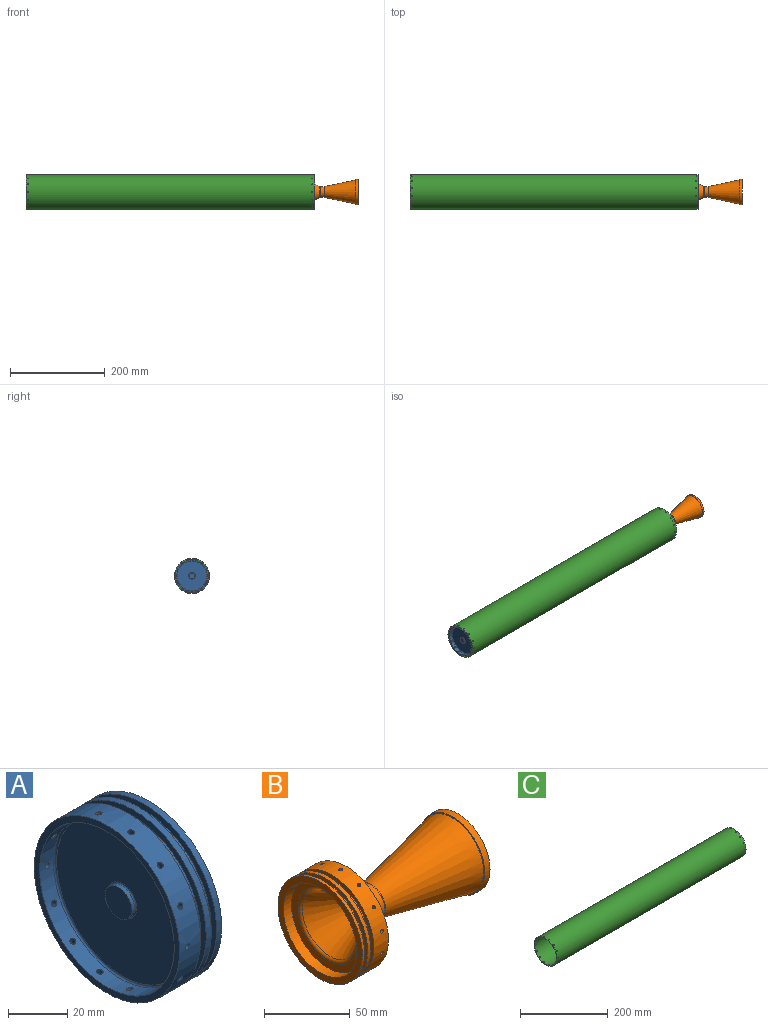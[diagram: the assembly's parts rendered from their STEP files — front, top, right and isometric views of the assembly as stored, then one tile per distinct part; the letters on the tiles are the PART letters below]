
ASSEMBLY  parts=3 mates=3
PART A: 61 faces, bbox 20.1x69.7x69.7 mm
  f0: cylinder r=34.72mm len=69.44mm, axis (-1,0,0), area 2150.1mm2, adj f1,f18,f19,f22,f25,f28,f31,f34
  f1: plane 69.44x69.44mm, normal (1,0,0), area 533.9mm2, adj f0,f2
  f2: cylinder r=32.18mm len=64.36mm, axis (-1,0,0), area 513.6mm2, adj f1,f3
  f3: plane 69.58x69.58mm, normal (-1,0,0), area 549.2mm2, adj f2,f4
  f4: cylinder r=34.79mm len=69.58mm, axis (-1,0,0), area 533mm2, adj f3,f5
  f5: plane 69.58x69.58mm, normal (1,0,0), area 549.2mm2, adj f4,f6
  f6: cylinder r=32.18mm len=64.36mm, axis (-1,0,0), area 513.6mm2, adj f5,f7
  f7: plane 69.58x69.58mm, normal (-1,0,0), area 549.2mm2, adj f6,f8
  f8: cylinder r=34.79mm len=69.58mm, axis (-1,0,0), area 533mm2, adj f7,f9
  f9: plane 69.58x69.58mm, normal (1,0,0), area 792.2mm2, adj f8,f10
  f10: cylinder r=30.96mm len=61.91mm, axis (-1,0,0), area 1842.7mm2, adj f9,f11
  f11: plane 61.91x61.91mm, normal (1,0,0), area 3010.6mm2, adj f10
  f12: plane 12.7x12.7mm, normal (-1,0,0), area 126.7mm2, adj f13
  f13: cylinder r=6.35mm len=12.7mm, axis (-1,0,0), area 55.7mm2, adj f12,f14
  f14: torus R=6.86mm, axis (-1,0,0), area 32.8mm2, adj f13,f15
  f15: plane 62.84x62.84mm, normal (-1,0,0), area 2953.6mm2, adj f14,f16
  f16: torus R=31.42mm, axis (-1,0,0), area 239.9mm2, adj f15,f17
  f17: cylinder r=32.18mm len=64.36mm, axis (-1,0,0), area 1291.1mm2, adj f16,f18,f20,f21,f23,f24,f26,f27
  f18: plane 69.44x69.44mm, normal (-1,0,0), area 533.9mm2, adj f0,f17
  f19: cylinder r=1.13mm len=2.54mm, axis (0,1,0), area 18mm2, adj f0,f20,f21
  f20: cone r=1.13mm half-angle=59deg, axis (0,1,0), area 0.1mm2, adj f17,f19
  f21: cone r=1.13mm half-angle=59deg, axis (0,1,0), area 0.1mm2, adj f17,f19
  f22: cylinder r=1.13mm len=3.27mm, axis (0,0.9,-0.43), area 18mm2, adj f0,f23,f24
  f23: cone r=1.13mm half-angle=59deg, axis (0,0.9,-0.43), area 0.1mm2, adj f17,f22
  f24: cone r=1.13mm half-angle=59deg, axis (0,0.9,-0.43), area 0.1mm2, adj f17,f22
  f25: cylinder r=1.13mm len=3.4mm, axis (0,0.62,-0.78), area 18mm2, adj f0,f26,f27
  f26: cone r=1.13mm half-angle=59deg, axis (0,0.62,-0.78), area 0.1mm2, adj f17,f25
  f27: cone r=1.13mm half-angle=59deg, axis (0,0.62,-0.78), area 0.1mm2, adj f17,f25
  f28: cylinder r=1.13mm len=2.98mm, axis (0,0.22,-0.97), area 18mm2, adj f0,f29,f30
  f29: cone r=1.13mm half-angle=59deg, axis (0,0.22,-0.97), area 0.1mm2, adj f17,f28
  f30: cone r=1.13mm half-angle=59deg, axis (0,0.22,-0.97), area 0.1mm2, adj f17,f28
  f31: cylinder r=1.13mm len=2.98mm, axis (0,-0.22,-0.97), area 18mm2, adj f0,f32,f33
  f32: cone r=1.13mm half-angle=59deg, axis (0,-0.22,-0.97), area 0.1mm2, adj f17,f31
  f33: cone r=1.13mm half-angle=59deg, axis (0,-0.22,-0.97), area 0.1mm2, adj f17,f31
  f34: cylinder r=1.13mm len=3.4mm, axis (0,-0.62,-0.78), area 18mm2, adj f0,f35,f36
  f35: cone r=1.13mm half-angle=59deg, axis (0,-0.62,-0.78), area 0.1mm2, adj f17,f34
  f36: cone r=1.13mm half-angle=59deg, axis (0,-0.62,-0.78), area 0.1mm2, adj f17,f34
  f37: cylinder r=1.13mm len=3.27mm, axis (0,-0.9,-0.43), area 18mm2, adj f0,f38,f39
  f38: cone r=1.13mm half-angle=59deg, axis (0,-0.9,-0.43), area 0.1mm2, adj f17,f37
  f39: cone r=1.13mm half-angle=59deg, axis (0,-0.9,-0.43), area 0.1mm2, adj f17,f37
  f40: cylinder r=1.13mm len=2.54mm, axis (0,-1,0), area 18mm2, adj f0,f41,f42
  f41: cone r=1.13mm half-angle=59deg, axis (0,-1,0), area 0.1mm2, adj f17,f40
  f42: cone r=1.13mm half-angle=59deg, axis (0,-1,0), area 0.1mm2, adj f17,f40
  f43: cylinder r=1.13mm len=3.27mm, axis (0,-0.9,0.43), area 18mm2, adj f0,f44,f45
  f44: cone r=1.13mm half-angle=59deg, axis (0,-0.9,0.43), area 0.1mm2, adj f17,f43
  f45: cone r=1.13mm half-angle=59deg, axis (0,-0.9,0.43), area 0.1mm2, adj f17,f43
  f46: cylinder r=1.13mm len=3.4mm, axis (0,-0.62,0.78), area 18mm2, adj f0,f47,f48
  f47: cone r=1.13mm half-angle=59deg, axis (0,-0.62,0.78), area 0.1mm2, adj f17,f46
  f48: cone r=1.13mm half-angle=59deg, axis (0,-0.62,0.78), area 0.1mm2, adj f17,f46
  f49: cylinder r=1.13mm len=2.98mm, axis (0,-0.22,0.97), area 18mm2, adj f0,f50,f51
  f50: cone r=1.13mm half-angle=59deg, axis (0,-0.22,0.97), area 0.1mm2, adj f17,f49
  f51: cone r=1.13mm half-angle=59deg, axis (0,-0.22,0.97), area 0.1mm2, adj f17,f49
  f52: cylinder r=1.13mm len=2.98mm, axis (0,0.22,0.97), area 18mm2, adj f0,f53,f54
  f53: cone r=1.13mm half-angle=59deg, axis (0,0.22,0.97), area 0.1mm2, adj f17,f52
  f54: cone r=1.13mm half-angle=59deg, axis (0,0.22,0.97), area 0.1mm2, adj f17,f52
  f55: cylinder r=1.13mm len=3.4mm, axis (0,0.62,0.78), area 18mm2, adj f0,f56,f57
  f56: cone r=1.13mm half-angle=59deg, axis (0,0.62,0.78), area 0.1mm2, adj f17,f55
  f57: cone r=1.13mm half-angle=59deg, axis (0,0.62,0.78), area 0.1mm2, adj f17,f55
  f58: cylinder r=1.13mm len=3.27mm, axis (0,0.9,0.43), area 18mm2, adj f0,f59,f60
  f59: cone r=1.13mm half-angle=59deg, axis (0,0.9,0.43), area 0.1mm2, adj f17,f58
  f60: cone r=1.13mm half-angle=59deg, axis (0,0.9,0.43), area 0.1mm2, adj f17,f58
PART B: 69 faces, bbox 113.5x69.5x69.5 mm
  f0: plane 69.52x69.52mm, normal (-1,0,0), area 923.2mm2, adj f1,f26
  f1: cylinder r=34.76mm len=69.52mm, axis (-1,0,0), area 416.1mm2, adj f0,f2
  f2: plane 69.52x69.52mm, normal (1,0,0), area 534.5mm2, adj f1,f3
  f3: cylinder r=32.22mm len=64.44mm, axis (-1,0,0), area 514.2mm2, adj f2,f4
  f4: plane 69.52x69.52mm, normal (-1,0,0), area 534.5mm2, adj f3,f5
  f5: cylinder r=34.76mm len=69.52mm, axis (-1,0,0), area 554.7mm2, adj f4,f6
  f6: plane 69.52x69.52mm, normal (1,0,0), area 534.5mm2, adj f5,f7
  f7: cylinder r=32.22mm len=64.44mm, axis (-1,0,0), area 514.2mm2, adj f6,f8
  f8: plane 69.52x69.52mm, normal (-1,0,0), area 534.5mm2, adj f7,f9
  f9: cylinder r=34.76mm len=69.52mm, axis (-1,0,0), area 2579.6mm2, adj f8,f10,f27,f30,f33,f36,f39,f42
  f10: plane 69.52x69.52mm, normal (1,0,0), area 534.5mm2, adj f9,f11
  f11: cylinder r=32.22mm len=64.44mm, axis (-1,0,0), area 1796.5mm2, adj f10,f12,f28,f29,f31,f32,f34,f35
  f12: plane 64.44x64.44mm, normal (1,0,0), area 1559.8mm2, adj f11,f13
  f13: cone r=11.76mm half-angle=30deg, axis (-1,0,0), area 2533.4mm2, adj f12,f14
  f14: torus R=13.96mm, axis (-1,0,0), area 96.4mm2, adj f13,f15
  f15: cylinder r=11.42mm len=22.85mm, axis (-1,0,0), area 589.8mm2, adj f14,f16
  f16: torus R=13.96mm, axis (-1,0,0), area 38.2mm2, adj f15,f17
  f17: cone r=25.66mm half-angle=12deg, axis (1,0,0), area 7961mm2, adj f16,f18
  f18: plane 53.11x53.11mm, normal (-1,0,0), area 145.9mm2, adj f17,f19
  f19: cylinder r=26.55mm len=53.11mm, axis (-1,0,0), area 724.7mm2, adj f18,f20
  f20: plane 53.11x53.11mm, normal (1,0,0), area 247mm2, adj f19,f21
  f21: cone r=8.14mm half-angle=12deg, axis (1,0,0), area 8464.8mm2, adj f20,f22
  f22: torus R=10.62mm, axis (-1,0,0), area 95.6mm2, adj f21,f23
  f23: cone r=22.48mm half-angle=30deg, axis (-1,0,0), area 2728.2mm2, adj f22,f24
  f24: torus R=24.68mm, axis (-1,0,0), area 392.1mm2, adj f23,f25
  f25: plane 60.48x60.48mm, normal (-1,0,0), area 959.6mm2, adj f24,f26
  f26: cylinder r=30.24mm len=60.48mm, axis (-1,0,0), area 1254.7mm2, adj f0,f25
  f27: cylinder r=1.13mm len=2.54mm, axis (0,0,1), area 18mm2, adj f9,f28,f29
  f28: cone r=1.13mm half-angle=59deg, axis (0,0,1), area 0.1mm2, adj f11,f27
  f29: cone r=1.13mm half-angle=59deg, axis (0,0,1), area 0.1mm2, adj f11,f27
  f30: cylinder r=1.13mm len=3.27mm, axis (0,0.43,0.9), area 18mm2, adj f9,f31,f32
  f31: cone r=1.13mm half-angle=59deg, axis (0,0.43,0.9), area 0.1mm2, adj f11,f30
  f32: cone r=1.13mm half-angle=59deg, axis (0,0.43,0.9), area 0.1mm2, adj f11,f30
  f33: cylinder r=1.13mm len=3.4mm, axis (0,0.78,0.62), area 18mm2, adj f9,f34,f35
  f34: cone r=1.13mm half-angle=59deg, axis (0,0.78,0.62), area 0.1mm2, adj f11,f33
  f35: cone r=1.13mm half-angle=59deg, axis (0,0.78,0.62), area 0.1mm2, adj f11,f33
  f36: cylinder r=1.13mm len=2.98mm, axis (0,0.97,0.22), area 18mm2, adj f9,f37,f38
  f37: cone r=1.13mm half-angle=59deg, axis (0,0.97,0.22), area 0.1mm2, adj f11,f36
  f38: cone r=1.13mm half-angle=59deg, axis (0,0.97,0.22), area 0.1mm2, adj f11,f36
  f39: cylinder r=1.13mm len=2.98mm, axis (0,0.97,-0.22), area 18mm2, adj f9,f40,f41
  f40: cone r=1.13mm half-angle=59deg, axis (0,0.97,-0.22), area 0.1mm2, adj f11,f39
  f41: cone r=1.13mm half-angle=59deg, axis (0,0.97,-0.22), area 0.1mm2, adj f11,f39
  f42: cylinder r=1.13mm len=3.4mm, axis (0,0.78,-0.62), area 18mm2, adj f9,f43,f44
  f43: cone r=1.13mm half-angle=59deg, axis (0,0.78,-0.62), area 0.1mm2, adj f11,f42
  f44: cone r=1.13mm half-angle=59deg, axis (0,0.78,-0.62), area 0.1mm2, adj f11,f42
  f45: cylinder r=1.13mm len=3.27mm, axis (0,0.43,-0.9), area 18mm2, adj f9,f46,f47
  f46: cone r=1.13mm half-angle=59deg, axis (0,0.43,-0.9), area 0.1mm2, adj f11,f45
  f47: cone r=1.13mm half-angle=59deg, axis (0,0.43,-0.9), area 0.1mm2, adj f11,f45
  f48: cylinder r=1.13mm len=2.54mm, axis (0,0,-1), area 18mm2, adj f9,f49,f50
  f49: cone r=1.13mm half-angle=59deg, axis (0,0,-1), area 0.1mm2, adj f11,f48
  f50: cone r=1.13mm half-angle=59deg, axis (0,0,-1), area 0.1mm2, adj f11,f48
  f51: cylinder r=1.13mm len=3.27mm, axis (0,-0.43,-0.9), area 18mm2, adj f9,f52,f53
  f52: cone r=1.13mm half-angle=59deg, axis (0,-0.43,-0.9), area 0.1mm2, adj f11,f51
  f53: cone r=1.13mm half-angle=59deg, axis (0,-0.43,-0.9), area 0.1mm2, adj f11,f51
  f54: cylinder r=1.13mm len=3.4mm, axis (0,-0.78,-0.62), area 18mm2, adj f9,f55,f56
  f55: cone r=1.13mm half-angle=59deg, axis (0,-0.78,-0.62), area 0.1mm2, adj f11,f54
  f56: cone r=1.13mm half-angle=59deg, axis (0,-0.78,-0.62), area 0.1mm2, adj f11,f54
  f57: cylinder r=1.13mm len=2.98mm, axis (0,-0.97,-0.22), area 18mm2, adj f9,f58,f59
  f58: cone r=1.13mm half-angle=59deg, axis (0,-0.97,-0.22), area 0.1mm2, adj f11,f57
  f59: cone r=1.13mm half-angle=59deg, axis (0,-0.97,-0.22), area 0.1mm2, adj f11,f57
  f60: cylinder r=1.13mm len=2.98mm, axis (0,-0.97,0.22), area 18mm2, adj f9,f61,f62
  f61: cone r=1.13mm half-angle=59deg, axis (0,-0.97,0.22), area 0.1mm2, adj f11,f60
  f62: cone r=1.13mm half-angle=59deg, axis (0,-0.97,0.22), area 0.1mm2, adj f11,f60
  f63: cylinder r=1.13mm len=3.4mm, axis (0,-0.78,0.62), area 18mm2, adj f9,f64,f65
  f64: cone r=1.13mm half-angle=59deg, axis (0,-0.78,0.62), area 0.1mm2, adj f11,f63
  f65: cone r=1.13mm half-angle=59deg, axis (0,-0.78,0.62), area 0.1mm2, adj f11,f63
  f66: cylinder r=1.13mm len=3.27mm, axis (0,-0.43,0.9), area 18mm2, adj f9,f67,f68
  f67: cone r=1.13mm half-angle=59deg, axis (0,-0.43,0.9), area 0.1mm2, adj f11,f66
  f68: cone r=1.13mm half-angle=59deg, axis (0,-0.43,0.9), area 0.1mm2, adj f11,f66
PART C: 32 faces, bbox 610x74x74 mm
  f0: plane 74x74mm, normal (-1,0,0), area 452.4mm2, adj f1,f3
  f1: cylinder r=37mm len=610mm, axis (-1,0,0), area 141700.8mm2, adj f0,f2,f4,f5,f6,f7,f8,f9
  f2: plane 74x74mm, normal (1,0,0), area 452.4mm2, adj f1,f3
  f3: cylinder r=35mm len=610mm, axis (-1,0,0), area 134035.2mm2, adj f0,f2,f4,f5,f6,f7,f8,f9
  f4: cylinder r=1.13mm len=2.26mm, axis (0,1,0), area 14.2mm2, adj f1,f3
  f5: cylinder r=1.13mm len=2.91mm, axis (0,0.9,-0.43), area 14.2mm2, adj f1,f3
  f6: cylinder r=1.13mm len=3.03mm, axis (0,0.62,-0.78), area 14.2mm2, adj f1,f3
  f7: cylinder r=1.13mm len=2.65mm, axis (0,0.22,-0.97), area 14.2mm2, adj f1,f3
  f8: cylinder r=1.13mm len=2.65mm, axis (0,-0.22,-0.97), area 14.2mm2, adj f1,f3
  f9: cylinder r=1.13mm len=3.03mm, axis (0,-0.62,-0.78), area 14.2mm2, adj f1,f3
  f10: cylinder r=1.13mm len=2.91mm, axis (0,-0.9,-0.43), area 14.2mm2, adj f1,f3
  f11: cylinder r=1.13mm len=2.26mm, axis (0,-1,0), area 14.2mm2, adj f1,f3
  f12: cylinder r=1.13mm len=2.91mm, axis (0,-0.9,0.43), area 14.2mm2, adj f1,f3
  f13: cylinder r=1.13mm len=3.03mm, axis (0,-0.62,0.78), area 14.2mm2, adj f1,f3
  f14: cylinder r=1.13mm len=2.65mm, axis (0,-0.22,0.97), area 14.2mm2, adj f1,f3
  f15: cylinder r=1.13mm len=2.65mm, axis (0,0.22,0.97), area 14.2mm2, adj f1,f3
  f16: cylinder r=1.13mm len=3.03mm, axis (0,0.62,0.78), area 14.2mm2, adj f1,f3
  f17: cylinder r=1.13mm len=2.91mm, axis (0,0.9,0.43), area 14.2mm2, adj f1,f3
  f18: cylinder r=1.13mm len=2.26mm, axis (0,1,0), area 14.2mm2, adj f1,f3
  f19: cylinder r=1.13mm len=2.91mm, axis (0,0.9,-0.43), area 14.2mm2, adj f1,f3
  f20: cylinder r=1.13mm len=3.03mm, axis (0,0.62,-0.78), area 14.2mm2, adj f1,f3
  f21: cylinder r=1.13mm len=2.65mm, axis (0,0.22,-0.97), area 14.2mm2, adj f1,f3
  f22: cylinder r=1.13mm len=2.65mm, axis (0,-0.22,-0.97), area 14.2mm2, adj f1,f3
  f23: cylinder r=1.13mm len=3.03mm, axis (0,-0.62,-0.78), area 14.2mm2, adj f1,f3
  f24: cylinder r=1.13mm len=2.91mm, axis (0,-0.9,-0.43), area 14.2mm2, adj f1,f3
  f25: cylinder r=1.13mm len=2.26mm, axis (0,-1,0), area 14.2mm2, adj f1,f3
  f26: cylinder r=1.13mm len=2.91mm, axis (0,-0.9,0.43), area 14.2mm2, adj f1,f3
  f27: cylinder r=1.13mm len=3.03mm, axis (0,-0.62,0.78), area 14.2mm2, adj f1,f3
  f28: cylinder r=1.13mm len=2.65mm, axis (0,-0.22,0.97), area 14.2mm2, adj f1,f3
  f29: cylinder r=1.13mm len=2.65mm, axis (0,0.22,0.97), area 14.2mm2, adj f1,f3
  f30: cylinder r=1.13mm len=3.03mm, axis (0,0.62,0.78), area 14.2mm2, adj f1,f3
  f31: cylinder r=1.13mm len=2.91mm, axis (0,0.9,0.43), area 14.2mm2, adj f1,f3
PLACE A t=(0,0,7.88)mm
PLACE B t=(623.42,0,7.88)mm
PLACE C t=(268.56,0,7.88)mm
MATE slider B.f1 <-> C.f1  axis (1,0,0) through (593.15,0,7.88)mm
MATE fastened C.f1 <-> C.f1  axis (-1,0,0) through (-17.01,0,7.88)mm
MATE slider C.f1 <-> A.f0  axis (-1,0,0) through (-17.01,0,7.88)mm
